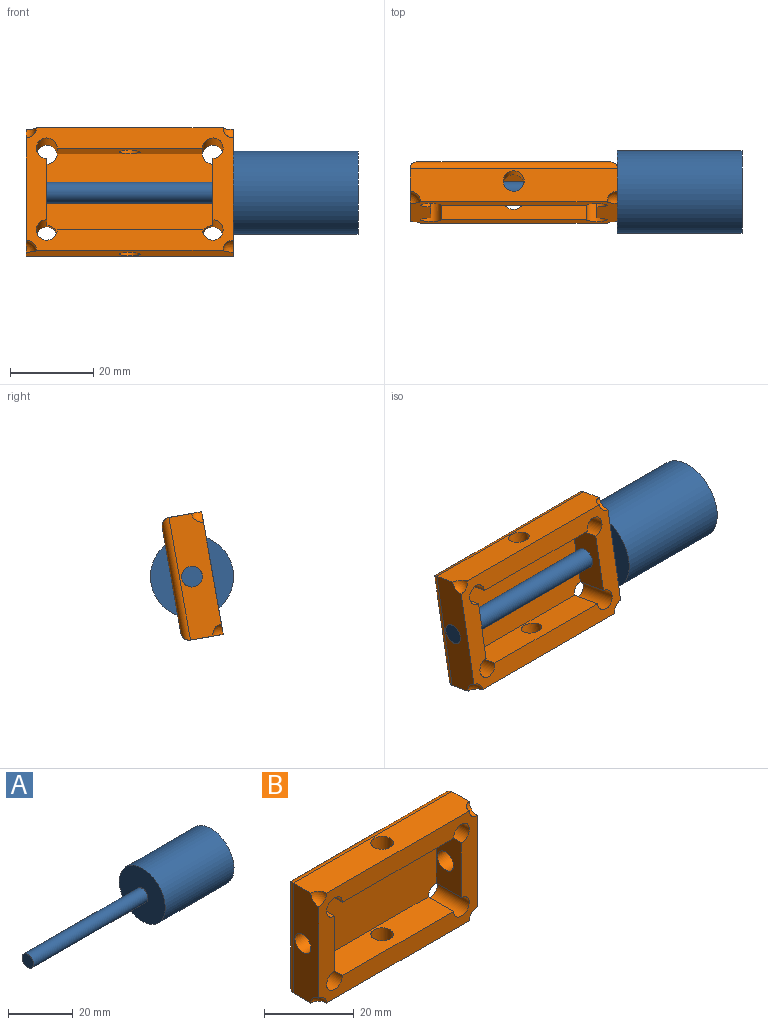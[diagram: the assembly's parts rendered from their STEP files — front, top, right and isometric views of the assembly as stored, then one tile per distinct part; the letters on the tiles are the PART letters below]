
ASSEMBLY  parts=2 mates=1
PART A: 5 faces, bbox 80x20x20 mm
  f0: cylinder r=2.5mm len=50mm, axis (-1,0,0), area 785.4mm2, adj f1,f3
  f1: plane 5x5mm, normal (-1,0,0), area 19.6mm2, adj f0
  f2: cylinder r=10mm len=30mm, axis (1,0,0), area 1885mm2, adj f3,f4
  f3: plane 20x20mm, normal (-1,0,0), area 294.5mm2, adj f0,f2
  f4: plane 20x20mm, normal (1,0,0), area 314.2mm2, adj f2
PART B: 27 faces, bbox 50x10x30 mm
  f0: cylinder r=2.5mm len=5mm, axis (0,0,1), area 78.5mm2, adj f5,f22
  f1: cylinder r=2.5mm len=10mm, axis (0,1,0), area 125.7mm2, adj f3,f11,f22,f24,f26
  f2: cylinder r=2.5mm len=10mm, axis (0,1,0), area 125.7mm2, adj f3,f11,f22,f25,f26
  f3: plane 50x30mm, normal (0,-1,0), area 621.5mm2, adj f1,f2,f5,f6,f7,f8,f9,f10
  f4: cylinder r=2.5mm len=5mm, axis (-1,0,0), area 78.5mm2, adj f10,f25
  f5: plane 50x8mm, normal (0,0,1), area 370.5mm2, adj f0,f3,f6,f10,f14,f16,f18
  f6: plane 30x8mm, normal (-1,0,0), area 210.5mm2, adj f3,f5,f7,f13,f16,f17,f19
  f7: plane 50x8mm, normal (0,0,-1), area 370.5mm2, adj f3,f6,f10,f12,f15,f17,f21
  f8: cylinder r=2.5mm len=10mm, axis (0,1,0), area 125.7mm2, adj f3,f11,f23,f24,f26
  f9: cylinder r=2.5mm len=10mm, axis (0,1,0), area 125.7mm2, adj f3,f11,f23,f25,f26
  f10: plane 30x8mm, normal (1,0,0), area 210.5mm2, adj f3,f4,f5,f7,f14,f15,f20
  f11: plane 46x26mm, normal (0,1,0), area 1117.5mm2, adj f1,f2,f8,f9,f18,f19,f20,f21
  f12: cylinder r=2.5mm len=5mm, axis (0,0,1), area 78.5mm2, adj f7,f23
  f13: cylinder r=2.5mm len=5mm, axis (-1,0,0), area 78.5mm2, adj f6,f24
  f14: sphere r=2.5mm, area 9.8mm2, adj f3,f5,f10
  f15: sphere r=2.5mm, area 9.8mm2, adj f3,f7,f10
  f16: sphere r=2.5mm, area 9.8mm2, adj f3,f5,f6
  f17: sphere r=2.5mm, area 9.8mm2, adj f3,f6,f7
  f18: cylinder r=2mm len=50mm, axis (-1,0,0), area 152.5mm2, adj f5,f11,f19,f20
  f19: cylinder r=2mm len=30mm, axis (0,0,-1), area 89.7mm2, adj f6,f11,f18,f21
  f20: cylinder r=2mm len=30mm, axis (0,0,1), area 89.7mm2, adj f10,f11,f18,f21
  f21: cylinder r=2mm len=50mm, axis (1,0,0), area 152.5mm2, adj f7,f11,f19,f20
  f22: plane 35x8mm, normal (0,0,-1), area 260.4mm2, adj f0,f1,f2,f3,f26
  f23: plane 35x8mm, normal (0,0,1), area 260.4mm2, adj f3,f8,f9,f12,f26
  f24: plane 15x8mm, normal (1,0,0), area 100.4mm2, adj f1,f3,f8,f13,f26
  f25: plane 15x8mm, normal (-1,0,0), area 100.4mm2, adj f2,f3,f4,f9,f26
  f26: plane 40x20mm, normal (0,-1,0), area 780.4mm2, adj f1,f2,f8,f9,f22,f23,f24,f25
PLACE A t=(0,-45.51,-23.57)mm fixed
PLACE B rot(axis=(-1,0,0),10deg) t=(0,-2.68,-0.64)mm
MATE revolute A.f0 <-> B.f4  axis (-1,0,0) through (0,-5,15)mm
